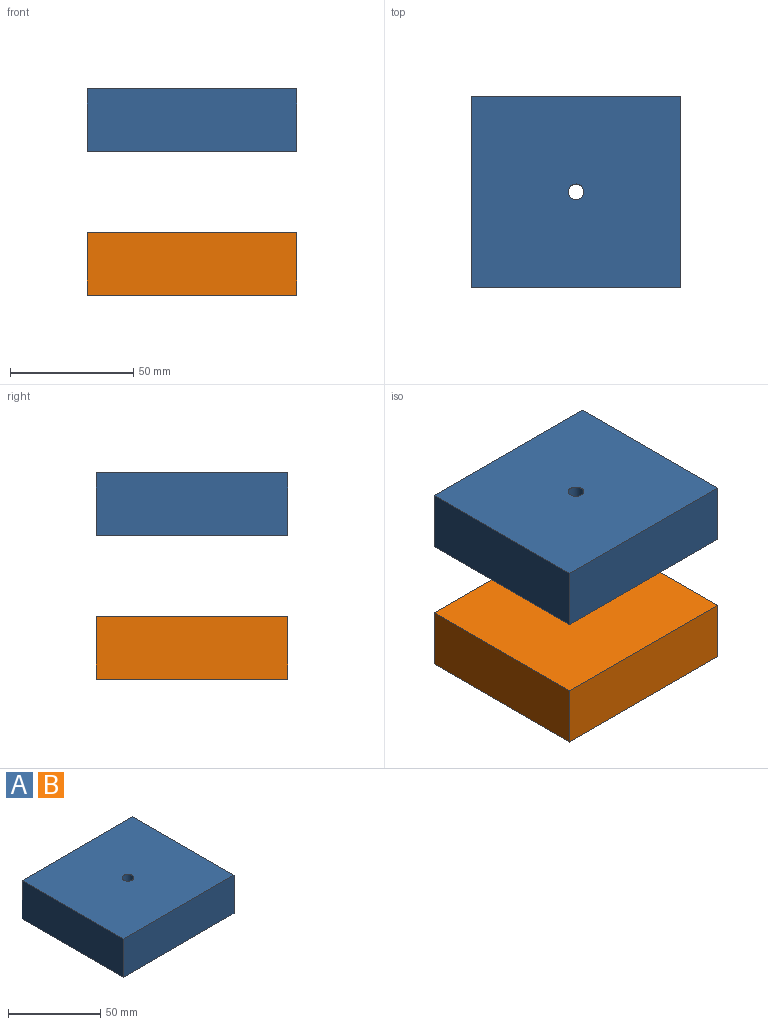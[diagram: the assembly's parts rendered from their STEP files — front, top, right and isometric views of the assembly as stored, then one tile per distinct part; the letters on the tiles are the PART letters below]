
ASSEMBLY  parts=2 mates=1
PART A: 9 faces, bbox 84.9x77.6x25.4 mm
  f0: plane 77.59x25.4mm, normal (-1,0,0), area 1970.7mm2, adj f1,f3,f4,f5
  f1: plane 84.92x25.4mm, normal (0,-1,0), area 2157mm2, adj f0,f2,f4,f5
  f2: plane 77.59x25.4mm, normal (1,0,0), area 1970.7mm2, adj f1,f3,f4,f5
  f3: plane 84.92x25.4mm, normal (0,1,0), area 2157mm2, adj f0,f2,f4,f5
  f4: plane 84.92x77.59mm, normal (0,0,1), area 6557.1mm2, adj f0,f1,f2,f3,f6
  f5: plane 84.92x77.59mm, normal (0,0,-1), area 6462.1mm2, adj f0,f1,f2,f3,f8
  f6: cylinder r=3.17mm len=19.05mm, axis (0,0,-1), area 380mm2, adj f4,f7
  f7: plane 12.7x12.7mm, normal (0,0,-1), area 95mm2, adj f6,f8
  f8: cylinder r=6.35mm len=12.7mm, axis (0,0,-1), area 253.4mm2, adj f5,f7
PART B: same geometry as A
PLACE A t=(-20.92,31.71,45.4)mm
PLACE B t=(-20.92,31.71,-12.87)mm fixed
MATE cylindrical B.f6 <-> A.f6  axis (0,0,1) through (-17.84,28.44,12.53)mm
